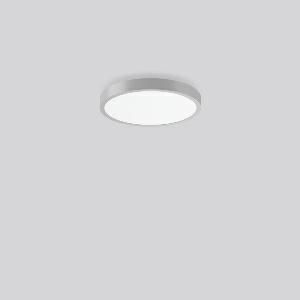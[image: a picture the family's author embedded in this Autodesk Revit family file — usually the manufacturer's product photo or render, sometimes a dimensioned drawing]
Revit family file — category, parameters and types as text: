
# Revit family: triona_round_a_312419_004_730_90fd
name_source: partatom
category: Lighting Fixtures
units: mm (PartAtom-declared; Revit-internal decimal feet)

## family parameters
Cut with Voids When Loaded = No
Host = Face
Light Source = No
Part Type = Normal
Room Calculation Point = No
Round Connector Dimension = Use Diameter
Shared = No

## types (1)
- TRIONA round A (1 x LED Modul 830, 4650 lm, 3000)
    Apparent Load = 48 VA
    CIE Flux Codes = 49 80 96 100 100
    Color Rendering = 80
    Color Temperature = 3000
    Default Elevation = 1800 mm
    Description = Series: TRIONA round
Decorative round LED surface-mounted luminaire. Flat, seamless frame: aluminium extrusion profile, powder coated. Cover made of sheet steel, powder-coated. Light emission through a diffuser: plastic, opal. Lightguide and diffuser made of non-yellowing plastic (PMMA). Lateral light emission (RZB SIDELITE technology) for above-average homogeneous light distribution. Suitable for Ceiling mounting, Wall (surface). Tool-free mounting via bayonet connection. Electronic ballast included. Very easy installation thanks to Plug+Play connection. With Casambi smart+free Bluetooth control for wireless network and operation using Android / iOS devices, free app available for download. 
Colour: silver, matt (approx. RAL 9006)
Diameter: 461 mm
Height: 88 mm
Lamp: LED
Socket: without socket
Colour temperature: 3000K
Colour rendering index (CRI): 80
System power: 48 W
Rated luminous flux: 4650 lm
Luminous efficiency: 97 lm/W
Control gear: Dimmable Bluetooth converter
Protection class: I
Type of protection: IP 20
    Height = 88 mm
    Lamp = 1 x LED Modul 830
    Lamp Light Flux = 4650 lm
    Lamp count = 1
    Length = 461 mm
    Lifetime = 50000 h
    Luminous efficacy = 97 lm/W
    Manufacturer = RZB
    ModVariant = No
    Model = 312419.004.730
    Mounting Place = Ceiling
    Mounting Type = Surface mounted
    Number of Poles = 1
    OnlyDefault = Yes
    Power Factor = 1
    Product Name = TRIONA round A
    Product group = Surface mounted modular luminaires
    ProductGroupID = 306
    Protection Class = Protection class I
    Protection Degree = IP 20
    RLX_Detail_Level = 1
    RLX_Emergency_Light_Flux = 0 lm
    RLX_Emergency_Type = 0
    RLX_Emergency_Type_DB = No
    RlxData = <blob elided: 27609 chars, md5=f2c169ea>
    Socket = socket
    Standby Power = 0 W
    System Light Flux = 4650 lm
    System Power = 48 W
    Type Comments = Product without accessories
    Type Image = 312420.004.jpg
    URL = http://relux.com
    VarID = ---
    Voltage = 230 V
    Voltage Range = 220-240 V
    Weight = 0.00 kg
    Width = 0 mm  [stored 0 ft]

note: [stored X ft] marks values corroborated as IEEE doubles in the binary element streams (Revit-internal decimal feet)

## geometry (parser evidence)
native form markers: Blend x4, Sweep x9
no freeform markers — native parametric forms only
